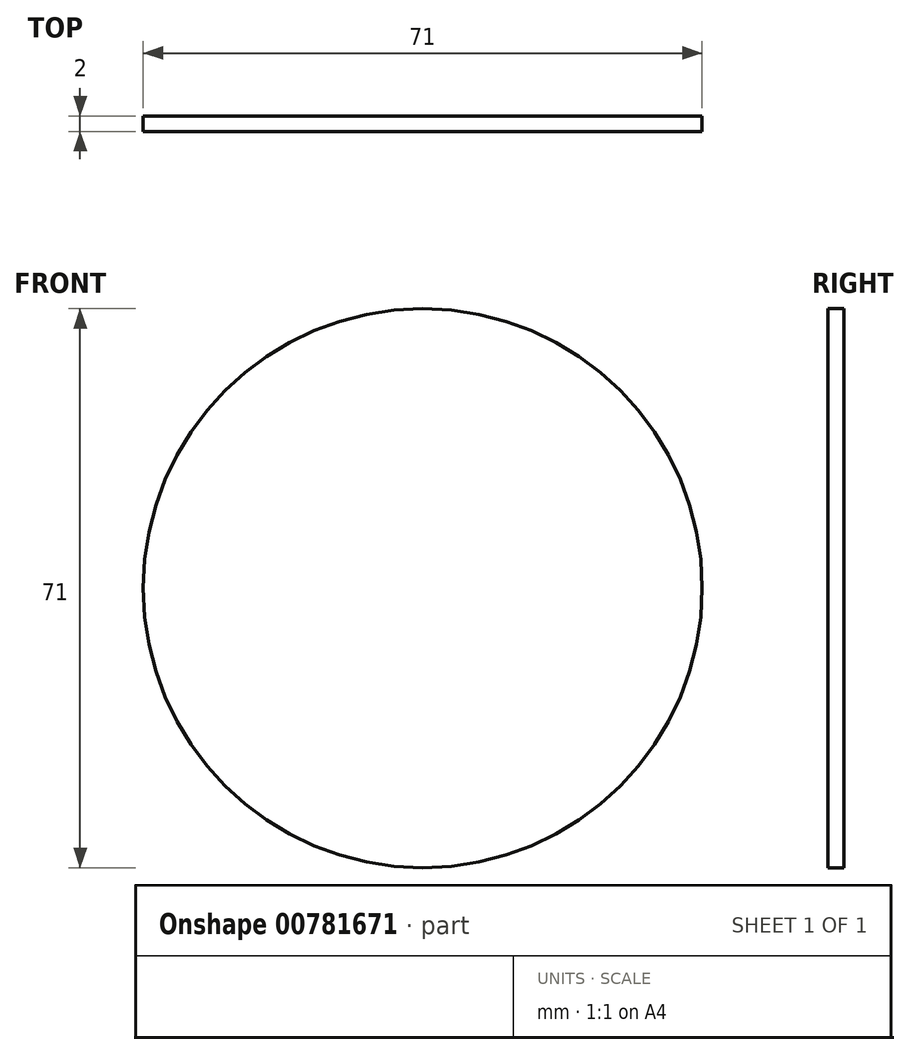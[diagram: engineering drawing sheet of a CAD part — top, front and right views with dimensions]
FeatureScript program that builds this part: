
annotation { "Feature Type Name" : "Feature", "Feature Type Description" : "" }
export const myFeature = defineFeature(function(context is Context, id is Id, definition is map)
    precondition{}
    {
        {
            var Q0;
            Q0=qCreatedBy(makeId("Front.planeOp"),FACE);
            var sketch = newSketch(context, id + "F0", { "sketchPlane" : qUnion([Q0])});
            skCircle(sketch, "E0", {"center": v(0, 0) * mm, "radius": 35.5 * mm});
            skSolve(sketch);
        }
        {
            var Q0;
            Q0=makeQuery(id+"F0.imprint","IMPRINT",FACE,{"disambiguationData":[TD([[makeQuery(id+"F0.imprint","IMPRINT",EDGE,{"derivedFrom":sQuery(id+"F0.wireOp",EDGE,"E0")}),1.0]])]});
            extrude(context, id + "F1", {"entities" : qUnion([Q0]), "depth" : 2 * mm, "offsetDistance" : 25.4 * mm});
        }
    });
